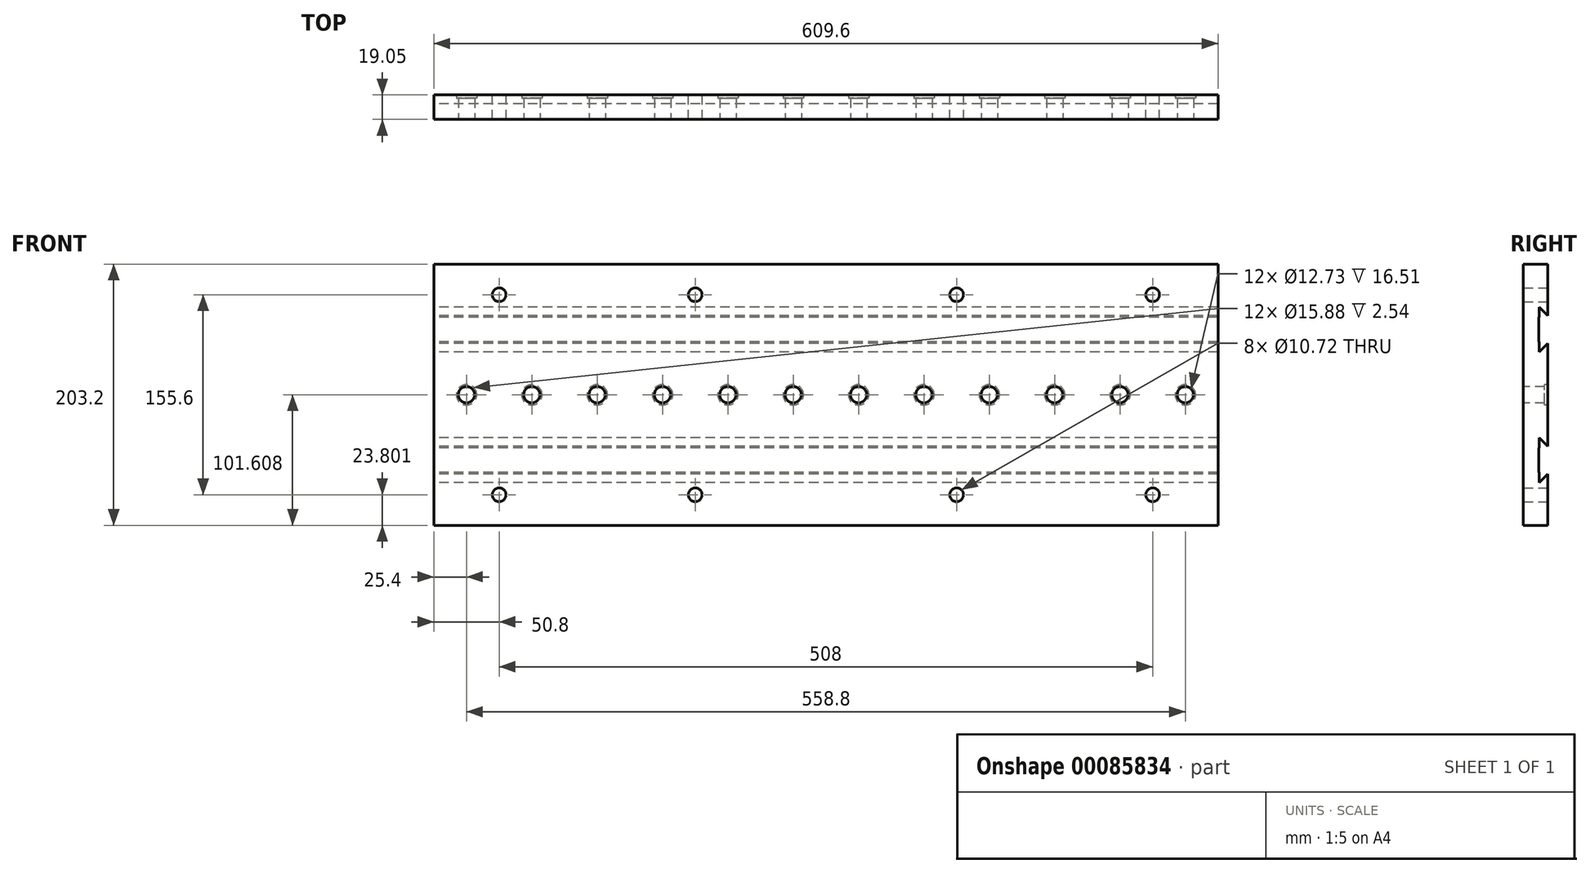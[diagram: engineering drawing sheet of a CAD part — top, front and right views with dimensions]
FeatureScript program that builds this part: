
annotation { "Feature Type Name" : "Feature", "Feature Type Description" : "" }
export const myFeature = defineFeature(function(context is Context, id is Id, definition is map)
    precondition{}
    {
        {
            var Q0;
            Q0=qCreatedBy(makeId("Right.planeOp"),FACE);
            var sketch = newSketch(context, id + "F0", { "sketchPlane" : qUnion([Q0])});
            skLineSegment(sketch, "E0.bottom", {"start": v(-51.24, 224.07) * mm, "end": v(-32.19, 224.07) * mm});
            skLineSegment(sketch, "E0.top", {"start": v(-51.24, 20.87) * mm, "end": v(-32.19, 20.87) * mm});
            skLineSegment(sketch, "E0.left", {"start": v(-51.24, 224.07) * mm, "end": v(-51.24, 20.87) * mm});
            skLineSegment(sketch, "E0.right", {"start": v(-32.19, 224.07) * mm, "end": v(-32.19, 184.02) * mm});
            skLineSegment(sketch, "E1", {"start": v(-38.92, 190.75) * mm, "end": v(-32.19, 184.02) * mm});
            skLineSegment(sketch, "E2", {"start": v(-38.92, 155.8) * mm, "end": v(-32.19, 162.54) * mm});
            skLineSegment(sketch, "E3.0", {"start": v(-39.17, 62.15) * mm, "end": v(-38.92, 62.15) * mm});
            skLineSegment(sketch, "E4.0", {"start": v(-39.17, 81.2) * mm, "end": v(-38.92, 81.2) * mm});
            skLineSegment(sketch, "E5", {"start": v(-38.92, 81.2) * mm, "end": v(-38.92, 81.2) * mm});
            skLineSegment(sketch, "E6", {"start": v(-38.92, 62.15) * mm, "end": v(-38.92, 54.2) * mm});
            skLineSegment(sketch, "E7.0", {"start": v(-39.17, 182.8) * mm, "end": v(-39.17, 163.75) * mm});
            skLineSegment(sketch, "E8.trimOffspring", {"start": v(-32.19, 60.94) * mm, "end": v(-32.19, 20.87) * mm});
            skLineSegment(sketch, "E9", {"start": v(-38.92, 155.8) * mm, "end": v(-38.92, 163.75) * mm});
            skLineSegment(sketch, "E10", {"start": v(-39.17, 163.75) * mm, "end": v(-38.92, 163.75) * mm});
            skLineSegment(sketch, "E11", {"start": v(-38.92, 182.8) * mm, "end": v(-39.17, 182.8) * mm});
            skLineSegment(sketch, "E12", {"start": v(-38.92, 81.2) * mm, "end": v(-38.92, 89.15) * mm});
            skLineSegment(sketch, "E13", {"start": v(-38.92, 89.15) * mm, "end": v(-32.19, 82.42) * mm});
            skLineSegment(sketch, "E14", {"start": v(-39.17, 81.2) * mm, "end": v(-39.17, 62.15) * mm});
            skLineSegment(sketch, "E15", {"start": v(-32.19, 60.94) * mm, "end": v(-38.92, 54.2) * mm});
            skLineSegment(sketch, "E16.trimOffspring", {"start": v(-32.19, 162.54) * mm, "end": v(-32.19, 82.42) * mm});
            skLineSegment(sketch, "E17.trimOffspring", {"start": v(-38.92, 190.75) * mm, "end": v(-38.92, 182.8) * mm});
            skSolve(sketch);
        }
        {
            var Q0;
            Q0=makeQuery(id+"F0.imprint","IMPRINT",FACE,{"disambiguationData":[TD([[makeQuery(id+"F0.imprint","IMPRINT",EDGE,{"derivedFrom":sQuery(id+"F0.wireOp",EDGE,"E0.bottom")}),-1.0]])]});
            extrude(context, id + "F1", {"entities" : qUnion([Q0]), "depth" : 609.6 * mm, "offsetDistance" : 25.4 * mm});
        }
        {
            var Q0;
            Q0=makeQuery(id+"F1.opExtrude","SWEPT_FACE",FACE,{"disambiguationData":[OSD([sQuery(id+"F0.wireOp",EDGE,"E0.left")])]});
            var sketch = newSketch(context, id + "F2", { "sketchPlane" : qUnion([Q0])});
            skPoint(sketch, "E18", {"position": v(50.8, 44.67) * mm});
            skPoint(sketch, "E19", {"position": v(203.2, 44.67) * mm});
            skPoint(sketch, "E20.MirrorP", {"position": v(50.8, 200.27) * mm});
            skPoint(sketch, "E21.MirrorP", {"position": v(203.2, 200.27) * mm});
            skPoint(sketch, "E22.MirrorP", {"position": v(406.4, 200.27) * mm});
            skPoint(sketch, "E23.MirrorP", {"position": v(558.8, 200.27) * mm});
            skPoint(sketch, "E24.MirrorP", {"position": v(558.8, 44.67) * mm});
            skPoint(sketch, "E25.MirrorP", {"position": v(406.4, 44.67) * mm});
            skLineSegment(sketch, "E26", {"start": v(0, 122.47) * mm, "end": v(609.6, 122.47) * mm});
            skPoint(sketch, "E27", {"position": v(25.4, 122.47) * mm});
            skPoint(sketch, "E28", {"position": v(76.2, 122.47) * mm});
            skPoint(sketch, "E29.1.0.0", {"position": v(127, 122.47) * mm});
            skPoint(sketch, "E29.2.0.0", {"position": v(177.8, 122.47) * mm});
            skPoint(sketch, "E29.3.0.0", {"position": v(228.6, 122.47) * mm});
            skPoint(sketch, "E29.4.0.0", {"position": v(279.4, 122.47) * mm});
            skPoint(sketch, "E29.5.0.0", {"position": v(330.2, 122.47) * mm});
            skPoint(sketch, "E29.6.0.0", {"position": v(381, 122.47) * mm});
            skPoint(sketch, "E29.7.0.0", {"position": v(431.8, 122.47) * mm});
            skPoint(sketch, "E29.8.0.0", {"position": v(482.6, 122.47) * mm});
            skPoint(sketch, "E29.9.0.0", {"position": v(533.4, 122.47) * mm});
            skPoint(sketch, "E29.10.0.0", {"position": v(584.2, 122.47) * mm});
            skLineSegment(sketch, "E29.direction1", {"start": v(76.2, 122.47) * mm, "end": v(127, 122.47) * mm, "construction": true});
            skSolve(sketch);
        }
        {
            var Q0;
            Q0=sQuery(id+"F2.wireOp",VERTEX,"E20.MirrorP");
            var Q1;
            Q1=sQuery(id+"F2.wireOp",VERTEX,"E21.MirrorP");
            var Q2;
            Q2=sQuery(id+"F2.wireOp",VERTEX,"E22.MirrorP");
            var Q3;
            Q3=sQuery(id+"F2.wireOp",VERTEX,"E23.MirrorP");
            var Q4;
            Q4=sQuery(id+"F2.wireOp",VERTEX,"E24.MirrorP");
            var Q5;
            Q5=sQuery(id+"F2.wireOp",VERTEX,"E25.MirrorP");
            var Q6;
            Q6=sQuery(id+"F2.wireOp",VERTEX,"E19");
            var Q7;
            Q7=sQuery(id+"F2.wireOp",VERTEX,"E18");
            var Q8;
            Q8=makeQuery(id+"F1.opExtrude","SWEPT_BODY",BODY,{"disambiguationData":[OSD([sQuery(id+"F0.wireOp",EDGE,"E0.bottom"),sQuery(id+"F0.wireOp",EDGE,"E0.top"),sQuery(id+"F0.wireOp",EDGE,"E0.left"),sQuery(id+"F0.wireOp",EDGE,"E0.right"),sQuery(id+"F0.wireOp",EDGE,"E1"),sQuery(id+"F0.wireOp",EDGE,"E2"),sQuery(id+"F0.wireOp",EDGE,"E3.0"),sQuery(id+"F0.wireOp",EDGE,"E4.0"),sQuery(id+"F0.wireOp",EDGE,"E6"),sQuery(id+"F0.wireOp",EDGE,"E7.0"),sQuery(id+"F0.wireOp",EDGE,"E8.trimOffspring"),sQuery(id+"F0.wireOp",EDGE,"E9"),sQuery(id+"F0.wireOp",EDGE,"E10"),sQuery(id+"F0.wireOp",EDGE,"E11"),sQuery(id+"F0.wireOp",EDGE,"E12"),sQuery(id+"F0.wireOp",EDGE,"E13"),sQuery(id+"F0.wireOp",EDGE,"E14"),sQuery(id+"F0.wireOp",EDGE,"E15"),sQuery(id+"F0.wireOp",EDGE,"E16.trimOffspring"),sQuery(id+"F0.wireOp",EDGE,"E17.trimOffspring")])]});
            hole(context, id + "F3", {"style" : HoleStyle.SIMPLE, "endStyle" : HoleEndStyle.THROUGH, "standardTappedOrClearance" : lookupTablePath({ "standard" : "ANSI", "engagement" : "75%", "pitch" : "13 tpi", "size" : "1/2", "type" : "Tapped" }), "standardBlindInLast" : lookupTablePath({ "standard" : "ANSI", "engagement" : "75%", "pitch" : "13 tpi", "size" : "1/2", "type" : "Tapped" }), "holeDiameter" : 10.72 * mm, "majorDiameter" : 12.7 * mm, "showTappedDepth" : true, "isTappedThrough" : true, "tappedDepth" : 19.05 * mm, "tapClearance" : 3, "locations" : qUnion([Q0, Q1, Q2, Q3, Q4, Q5, Q6, Q7]), "scope" : qUnion([Q8])});
        }
        {
            var Q0;
            Q0=makeQuery(id+"F1.opExtrude","SWEPT_FACE",FACE,{"disambiguationData":[OSD([sQuery(id+"F0.wireOp",EDGE,"E16.trimOffspring")])]});
            var sketch = newSketch(context, id + "F4", { "sketchPlane" : qUnion([Q0])});
            skSolve(sketch);
        }
        {
            var Q0;
            {var subQ0=sQuery(id+"F0.wireOp",EDGE,"E16.trimOffspring");Q0=makeQuery(id+"F4.imprint","IMPRINT",FACE,{"disambiguationData":[TD([[makeQuery(id+"F4.imprint","IMPRINT",EDGE,{"derivedFrom":makeQuery(id+"F1.opExtrude","CAP_EDGE",EDGE,{"disambiguationData":[OSD([subQ0])],"isStart":true})}),-1.0]])]});}
            var sketch = newSketch(context, id + "F5", { "sketchPlane" : qUnion([Q0])});
            skLineSegment(sketch, "E30.bottom", {"start": v(0, 162.54) * mm, "end": v(-609.6, 162.54) * mm});
            skLineSegment(sketch, "E30.top", {"start": v(0, 82.42) * mm, "end": v(-609.6, 82.42) * mm});
            skLineSegment(sketch, "E30.left", {"start": v(0, 162.54) * mm, "end": v(0, 82.42) * mm});
            skLineSegment(sketch, "E30.right", {"start": v(-609.6, 162.54) * mm, "end": v(-609.6, 82.42) * mm});
            skLineSegment(sketch, "E31", {"start": v(-609.6, 122.48) * mm, "end": v(0, 122.48) * mm});
            skPoint(sketch, "E32", {"position": v(-584.2, 122.48) * mm});
            skPoint(sketch, "E33.1.0.0", {"position": v(-533.4, 122.48) * mm});
            skPoint(sketch, "E33.2.0.0", {"position": v(-482.6, 122.48) * mm});
            skPoint(sketch, "E33.3.0.0", {"position": v(-431.8, 122.48) * mm});
            skPoint(sketch, "E33.4.0.0", {"position": v(-381, 122.48) * mm});
            skPoint(sketch, "E33.5.0.0", {"position": v(-330.2, 122.48) * mm});
            skPoint(sketch, "E33.6.0.0", {"position": v(-279.4, 122.48) * mm});
            skPoint(sketch, "E33.7.0.0", {"position": v(-228.6, 122.48) * mm});
            skPoint(sketch, "E33.8.0.0", {"position": v(-177.8, 122.48) * mm});
            skPoint(sketch, "E33.9.0.0", {"position": v(-127, 122.48) * mm});
            skPoint(sketch, "E33.10.0.0", {"position": v(-76.2, 122.48) * mm});
            skLineSegment(sketch, "E33.direction1", {"start": v(-584.2, 122.48) * mm, "end": v(-533.4, 122.48) * mm, "construction": true});
            skPoint(sketch, "E34.0.11.0", {"position": v(-25.4, 122.48) * mm});
            skSolve(sketch);
        }
        {
            var Q0;
            Q0=sQuery(id+"F5.wireOp",VERTEX,"E32");
            var Q1;
            Q1=sQuery(id+"F5.wireOp",VERTEX,"E33.1.0.0");
            var Q2;
            Q2=sQuery(id+"F5.wireOp",VERTEX,"E33.2.0.0");
            var Q3;
            Q3=sQuery(id+"F5.wireOp",VERTEX,"E33.4.0.0");
            var Q4;
            Q4=sQuery(id+"F5.wireOp",VERTEX,"E33.5.0.0");
            var Q5;
            Q5=sQuery(id+"F5.wireOp",VERTEX,"E33.6.0.0");
            var Q6;
            Q6=sQuery(id+"F5.wireOp",VERTEX,"E33.7.0.0");
            var Q7;
            Q7=sQuery(id+"F5.wireOp",VERTEX,"E33.8.0.0");
            var Q8;
            Q8=sQuery(id+"F5.wireOp",VERTEX,"E33.9.0.0");
            var Q9;
            Q9=sQuery(id+"F5.wireOp",VERTEX,"E33.10.0.0");
            var Q10;
            Q10=sQuery(id+"F5.wireOp",VERTEX,"E33.3.0.0");
            var Q11;
            Q11=sQuery(id+"F5.wireOp",VERTEX,"E34.0.11.0");
            var Q12;
            Q12=makeQuery(id+"F1.opExtrude","SWEPT_BODY",BODY,{"disambiguationData":[OSD([sQuery(id+"F0.wireOp",EDGE,"E0.bottom"),sQuery(id+"F0.wireOp",EDGE,"E0.top"),sQuery(id+"F0.wireOp",EDGE,"E0.left"),sQuery(id+"F0.wireOp",EDGE,"E0.right"),sQuery(id+"F0.wireOp",EDGE,"E1"),sQuery(id+"F0.wireOp",EDGE,"E2"),sQuery(id+"F0.wireOp",EDGE,"E3.0"),sQuery(id+"F0.wireOp",EDGE,"E4.0"),sQuery(id+"F0.wireOp",EDGE,"E6"),sQuery(id+"F0.wireOp",EDGE,"E7.0"),sQuery(id+"F0.wireOp",EDGE,"E8.trimOffspring"),sQuery(id+"F0.wireOp",EDGE,"E9"),sQuery(id+"F0.wireOp",EDGE,"E10"),sQuery(id+"F0.wireOp",EDGE,"E11"),sQuery(id+"F0.wireOp",EDGE,"E12"),sQuery(id+"F0.wireOp",EDGE,"E13"),sQuery(id+"F0.wireOp",EDGE,"E14"),sQuery(id+"F0.wireOp",EDGE,"E15"),sQuery(id+"F0.wireOp",EDGE,"E16.trimOffspring"),sQuery(id+"F0.wireOp",EDGE,"E17.trimOffspring")])]});
            hole(context, id + "F6", {"style" : HoleStyle.C_BORE, "endStyle" : HoleEndStyle.THROUGH, "holeDiameter" : 12.73 * mm, "cBoreDiameter" : 15.88 * mm, "cBoreDepth" : 2.54 * mm, "majorDiameter" : 6.35 * mm, "isTappedThrough" : true, "tappedDepth" : 19.05 * mm, "tapClearance" : 3, "startFromSketch" : true, "locations" : qUnion([Q0, Q1, Q2, Q3, Q4, Q5, Q6, Q7, Q8, Q9, Q10, Q11]), "scope" : qUnion([Q12])});
        }
    });
